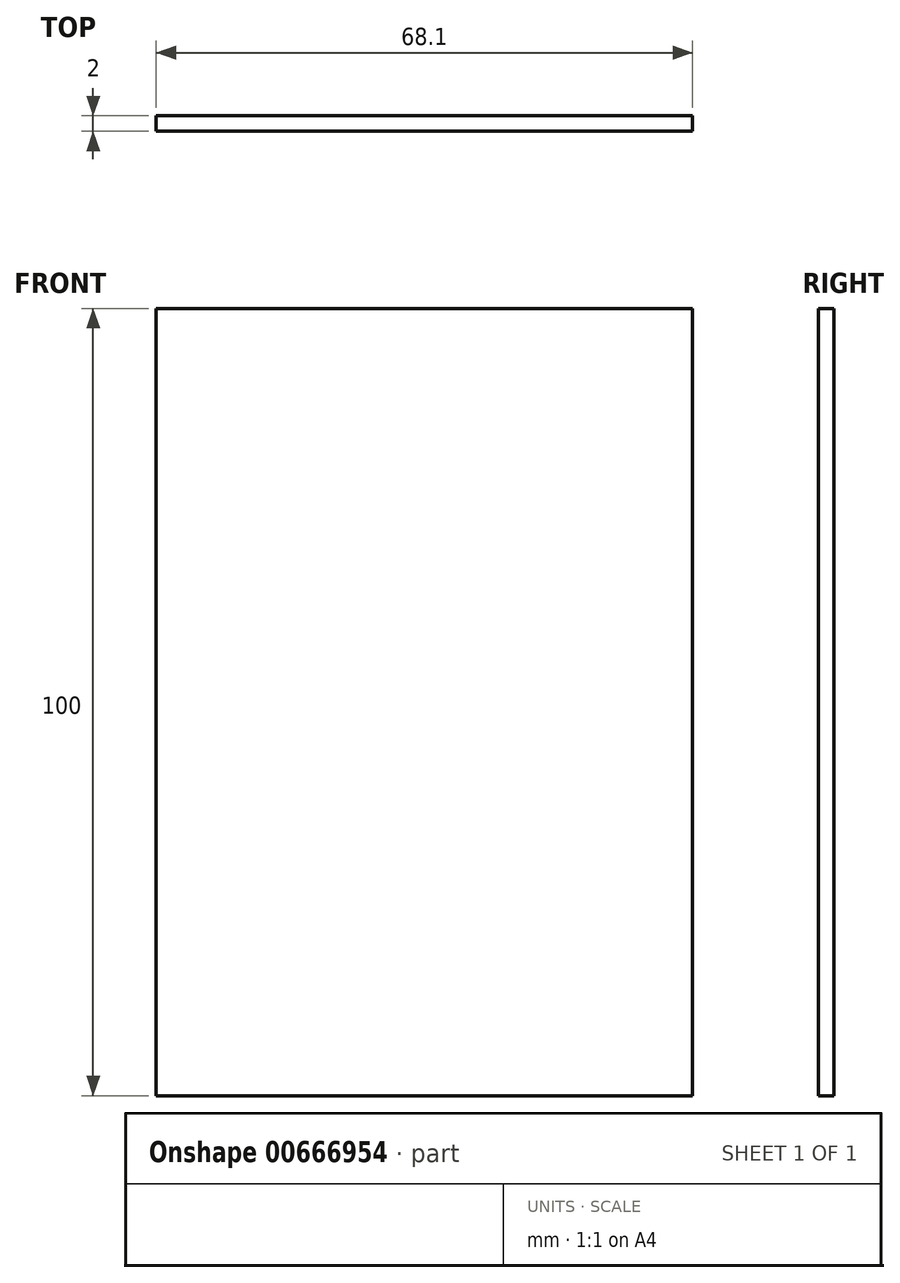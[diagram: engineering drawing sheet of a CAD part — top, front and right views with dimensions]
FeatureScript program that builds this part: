
annotation { "Feature Type Name" : "Feature", "Feature Type Description" : "" }
export const myFeature = defineFeature(function(context is Context, id is Id, definition is map)
    precondition{}
    {
        {
            var Q0;
            Q0=qCreatedBy(makeId("Front.planeOp"),FACE);
            var sketch = newSketch(context, id + "F0", { "sketchPlane" : qUnion([Q0])});
            skLineSegment(sketch, "E0", {"start": v(0, 0) * mm, "end": v(68.1, 0) * mm});
            skLineSegment(sketch, "E1", {"start": v(0, 0) * mm, "end": v(0, 100) * mm});
            skLineSegment(sketch, "E2", {"start": v(68.1, 0) * mm, "end": v(68.1, 100) * mm});
            skLineSegment(sketch, "E3", {"start": v(0, 100) * mm, "end": v(68.1, 100) * mm});
            skSolve(sketch);
        }
        {
            var Q0;
            Q0=makeQuery(id+"F0.imprint","IMPRINT",FACE,{"disambiguationData":[TD([[makeQuery(id+"F0.imprint","IMPRINT",EDGE,{"derivedFrom":sQuery(id+"F0.wireOp",EDGE,"E0")}),1.0]])]});
            extrude(context, id + "F1", {"entities" : qUnion([Q0]), "depth" : 2 * mm, "offsetDistance" : 25 * mm});
        }
    });
